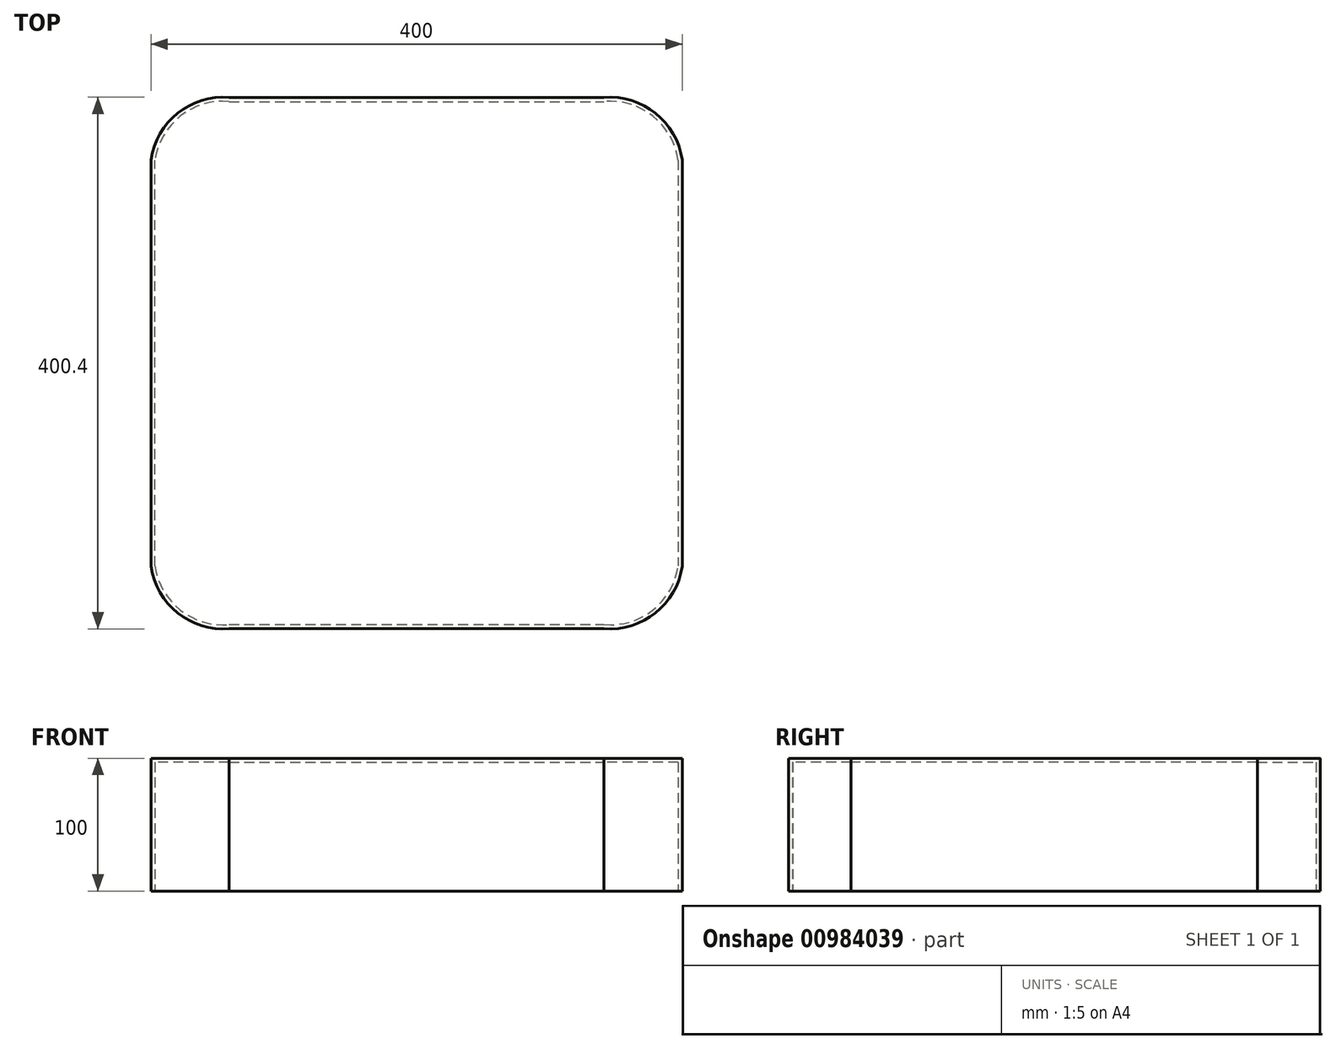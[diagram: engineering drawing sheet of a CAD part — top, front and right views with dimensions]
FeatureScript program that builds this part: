
annotation { "Feature Type Name" : "Feature", "Feature Type Description" : "" }
export const myFeature = defineFeature(function(context is Context, id is Id, definition is map)
    precondition{}
    {
        {
            var Q0;
            Q0=qCreatedBy(makeId("Top.planeOp"),FACE);
            var sketch = newSketch(context, id + "F0", { "sketchPlane" : qUnion([Q0])});
            skPoint(sketch, "E0.middle", {"position": v(0, 0) * mm});
            skLineSegment(sketch, "E1", {"start": v(0, 200) * mm, "end": v(0, -200) * mm, "construction": true});
            skLineSegment(sketch, "E2", {"start": v(-200, 0) * mm, "end": v(200, 0) * mm, "construction": true});
            skArc(sketch, "E3", {"start": v(-141.06, 200) * mm, "mid": v(-179.9, 188.24) * mm, "end": v(-200, 152.99) * mm});
            skArc(sketch, "E4.MirrorCS", {"start": v(-141.06, -200) * mm, "mid": v(-179.9, -188.24) * mm, "end": v(-200, -152.99) * mm});
            skLineSegment(sketch, "E5.MirrorCS", {"start": v(0, -200) * mm, "end": v(0, 200) * mm, "construction": true});
            skArc(sketch, "E6.MirrorCS", {"start": v(141.06, 200) * mm, "mid": v(179.9, 188.24) * mm, "end": v(200, 152.99) * mm});
            skArc(sketch, "E7.MirrorCS", {"start": v(141.06, -200) * mm, "mid": v(179.9, -188.24) * mm, "end": v(200, -152.99) * mm});
            skLineSegment(sketch, "E8", {"start": v(-141.06, 200) * mm, "end": v(141.06, 200) * mm});
            skLineSegment(sketch, "E9", {"start": v(200, 152.99) * mm, "end": v(200, -152.99) * mm});
            skLineSegment(sketch, "E10", {"start": v(-141.06, -200) * mm, "end": v(141.06, -200) * mm});
            skLineSegment(sketch, "E11", {"start": v(-200, -152.99) * mm, "end": v(-200, 152.99) * mm});
            skSolve(sketch);
        }
        {
            var Q0;
            Q0 = qSketchRegion(id + "F0", true);
            extrude(context, id + "F1", {"entities" : qUnion([Q0]), "depth" : 100 * mm, "offsetDistance" : 25.4 * mm});
        }
        {
            var Q0;
            Q0=qCreatedBy(makeId("Front.planeOp"),FACE);
            cPlane(context, id + "F2", {"entities" : qUnion([Q0]), "cplaneType" : CPlaneType.OFFSET, "offset" : 200 * mm, "width" : 150 * mm, "height" : 150 * mm});
        }
        {
            var Q0;
            Q0=makeQuery(id+"F1.opExtrude","CAP_FACE",FACE,{"disambiguationData":[OSD([sQuery(id+"F0.wireOp",EDGE,"E4.MirrorCS"),sQuery(id+"F0.wireOp",EDGE,"E3"),sQuery(id+"F0.wireOp",EDGE,"E6.MirrorCS"),sQuery(id+"F0.wireOp",EDGE,"E7.MirrorCS"),sQuery(id+"F0.wireOp",EDGE,"E8"),sQuery(id+"F0.wireOp",EDGE,"E9"),sQuery(id+"F0.wireOp",EDGE,"E10"),sQuery(id+"F0.wireOp",EDGE,"E11")])],"isStart":true});
            shell(context, id + "F3", {"entities" : qUnion([Q0]), "thickness" : 3 * mm});
        }
    });
